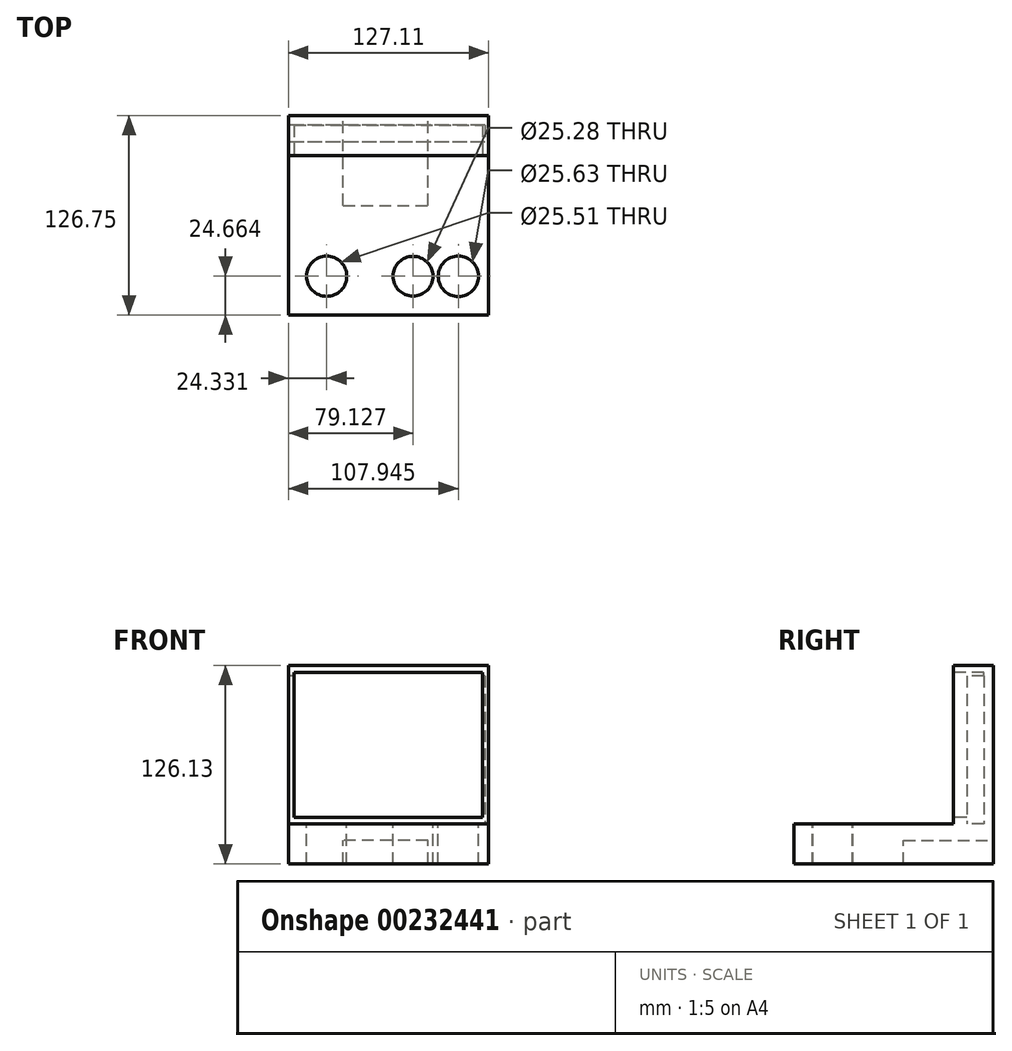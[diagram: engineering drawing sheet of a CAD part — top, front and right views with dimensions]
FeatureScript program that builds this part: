
annotation { "Feature Type Name" : "Feature", "Feature Type Description" : "" }
export const myFeature = defineFeature(function(context is Context, id is Id, definition is map)
    precondition{}
    {
        {
            var Q0;
            Q0=qCreatedBy(makeId("Front.planeOp"),FACE);
            var sketch = newSketch(context, id + "F0", { "sketchPlane" : qUnion([Q0])});
            skLineSegment(sketch, "E0", {"start": v(-60.05, -58.06) * mm, "end": v(67.06, -58.06) * mm});
            skLineSegment(sketch, "E1", {"start": v(67.06, -58.06) * mm, "end": v(67.06, -32.77) * mm});
            skLineSegment(sketch, "E2", {"start": v(67.06, -32.77) * mm, "end": v(-60.05, -32.77) * mm});
            skLineSegment(sketch, "E3", {"start": v(-60.05, -32.77) * mm, "end": v(-60.05, -58.06) * mm});
            skSolve(sketch);
        }
        {
            var Q0;
            Q0 = qSketchRegion(id + "F0", true);
            extrude(context, id + "F1", {"entities" : qUnion([Q0]), "oppositeDirection" : true, "depth" : 126.75 * mm});
        }
        {
            var Q0;
            Q0=makeQuery(id+"F1.opExtrude","CAP_FACE",FACE,{"disambiguationData":[OSD([sQuery(id+"F0.wireOp",EDGE,"E0"),sQuery(id+"F0.wireOp",EDGE,"E1"),sQuery(id+"F0.wireOp",EDGE,"E2"),sQuery(id+"F0.wireOp",EDGE,"E3")])],"isStart":false});
            var sketch = newSketch(context, id + "F2", { "sketchPlane" : qUnion([Q0])});
            skLineSegment(sketch, "E4.bottom", {"start": v(-28.65, -58.06) * mm, "end": v(25.3, -58.06) * mm});
            skLineSegment(sketch, "E4.top", {"start": v(-28.65, -43.13) * mm, "end": v(25.3, -43.13) * mm});
            skLineSegment(sketch, "E4.left", {"start": v(-28.65, -58.06) * mm, "end": v(-28.65, -43.13) * mm});
            skLineSegment(sketch, "E4.right", {"start": v(25.3, -58.06) * mm, "end": v(25.3, -43.13) * mm});
            skSolve(sketch);
        }
        {
            var Q0;
            Q0 = qSketchRegion(id + "F2", true);
            extrude(context, id + "F3", {"entities" : qUnion([Q0]), "operationType" : NewBodyOperationType.REMOVE, "oppositeDirection" : true, "depth" : 57.15 * mm});
        }
        {
            var Q0;
            Q0=makeQuery(id+"F1.opExtrude","SWEPT_FACE",FACE,{"disambiguationData":[OSD([sQuery(id+"F0.wireOp",EDGE,"E2")])]});
            var sketch = newSketch(context, id + "F4", { "sketchPlane" : qUnion([Q0])});
            skLineSegment(sketch, "E5.bottom", {"start": v(-60.05, 126.75) * mm, "end": v(67.06, 126.75) * mm});
            skLineSegment(sketch, "E5.top", {"start": v(-60.05, 101.38) * mm, "end": v(67.06, 101.38) * mm});
            skLineSegment(sketch, "E5.left", {"start": v(-60.05, 126.75) * mm, "end": v(-60.05, 101.38) * mm});
            skLineSegment(sketch, "E5.right", {"start": v(67.06, 126.75) * mm, "end": v(67.06, 101.38) * mm});
            skSolve(sketch);
        }
        {
            var Q0;
            Q0 = qSketchRegion(id + "F4", true);
            extrude(context, id + "F5", {"entities" : qUnion([Q0]), "operationType" : NewBodyOperationType.ADD, "depth" : 100.84 * mm});
        }
        {
            var Q0;
            Q0=makeQuery(id+"F5.boolean.opBoolean","MERGE",FACE,{"derivedFrom":[makeQuery(id+"F1.opExtrude","SWEPT_FACE",FACE,{"disambiguationData":[OSD([sQuery(id+"F0.wireOp",EDGE,"E3")])]}),makeQuery(id+"F5.opExtrude","SWEPT_FACE",FACE,{"disambiguationData":[OSD([sQuery(id+"F4.wireOp",EDGE,"E5.left")])]})]});
            var sketch = newSketch(context, id + "F6", { "sketchPlane" : qUnion([Q0])});
            skLineSegment(sketch, "E6.bottom", {"start": v(-120.68, 61.42) * mm, "end": v(-110, 61.42) * mm});
            skLineSegment(sketch, "E6.top", {"start": v(-120.68, -32.77) * mm, "end": v(-110, -32.77) * mm});
            skLineSegment(sketch, "E6.left", {"start": v(-120.68, 61.42) * mm, "end": v(-120.68, -32.77) * mm});
            skLineSegment(sketch, "E6.right", {"start": v(-110, 61.42) * mm, "end": v(-110, -32.77) * mm});
            skSolve(sketch);
        }
        {
            var Q0;
            Q0 = qSketchRegion(id + "F6", true);
            extrude(context, id + "F7", {"entities" : qUnion([Q0]), "operationType" : NewBodyOperationType.REMOVE, "oppositeDirection" : true, "depth" : 124.97 * mm});
        }
        {
            var Q0;
            Q0=makeQuery(id+"F5.opExtrude","SWEPT_FACE",FACE,{"disambiguationData":[OSD([sQuery(id+"F4.wireOp",EDGE,"E5.top")])]});
            var sketch = newSketch(context, id + "F8", { "sketchPlane" : qUnion([Q0])});
            skLineSegment(sketch, "E7.bottom", {"start": v(-56.39, -28.5) * mm, "end": v(63.1, -28.5) * mm});
            skLineSegment(sketch, "E7.top", {"start": v(-56.39, 63.55) * mm, "end": v(63.1, 63.55) * mm});
            skLineSegment(sketch, "E7.left", {"start": v(-56.39, -28.5) * mm, "end": v(-56.39, 63.55) * mm});
            skLineSegment(sketch, "E7.right", {"start": v(63.1, -28.5) * mm, "end": v(63.1, 63.55) * mm});
            skSolve(sketch);
        }
        {
            var Q0;
            Q0 = qSketchRegion(id + "F8", true);
            extrude(context, id + "F9", {"entities" : qUnion([Q0]), "operationType" : NewBodyOperationType.REMOVE, "oppositeDirection" : true, "depth" : 19.3 * mm});
        }
        {
            var Q0;
            Q0=makeQuery(id+"F1.opExtrude","SWEPT_FACE",FACE,{"disambiguationData":[OSD([sQuery(id+"F0.wireOp",EDGE,"E2")])]});
            var sketch = newSketch(context, id + "F10", { "sketchPlane" : qUnion([Q0])});
            skCircle(sketch, "E8", {"center": v(19.08, 24.66) * mm, "radius": 12.64 * mm});
            skCircle(sketch, "E9", {"center": v(47.9, 24.66) * mm, "radius": 12.82 * mm});
            skCircle(sketch, "E10", {"center": v(-35.72, 24.66) * mm, "radius": 12.75 * mm});
            skSolve(sketch);
        }
        {
            var Q0;
            Q0 = qSketchRegion(id + "F10", true);
            extrude(context, id + "F11", {"entities" : qUnion([Q0]), "operationType" : NewBodyOperationType.REMOVE, "oppositeDirection" : true, "depth" : 25.4 * mm});
        }
    });
